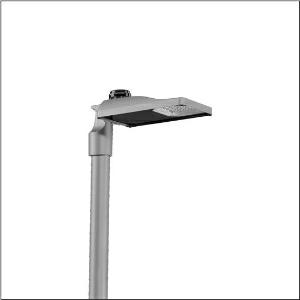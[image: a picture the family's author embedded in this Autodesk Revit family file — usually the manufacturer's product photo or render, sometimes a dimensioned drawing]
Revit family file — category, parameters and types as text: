
# Revit family: streetlight_sl_31_micro___st1_5a_5xh1p7bn08ca_d18d
name_source: partatom
category: Lighting Fixtures
units: mm (PartAtom-declared; Revit-internal decimal feet)

## family parameters
Cut with Voids When Loaded = No
Host = Face
Light Source = No
Part Type = Normal
Room Calculation Point = No
Round Connector Dimension = Use Diameter
Shared = No

## types (1)
- --- (1 x LED, 1150 lm, 10.3 W, 2200K)
    Apparent Load = 10 VA
    CIE Flux Codes = 22 53 95 100 100
    Color Rendering = 70
    Color Temperature = 2200K
    Default Elevation = 1800 mm
    Description = Streetlight SL 31 micro NEMA (7pin) mast luminaire for post-top, side-entry; light control with lens of PMMA; light distribution: ST1.5a, direct asymmetric distribution, for standard-compliant lighting for roads and squares; LED: luminous flux: 1.150lm, light colour: 722, colour temperature: 2200K; luminous efficacy: 111,7lm/W; control: overheat protection, intelligent temperature release in ECG and LED module, constant luminous flux control, time-dependent luminous flux control, flexible luminous flux parameterisation, pre-setting: linear dimming characteristic; luminaire housing, of diecast aluminium, SITECO metallic grey (DB 702S), corrosivity category C5 high according to DIN EN ISO 12944; cover of toughened safety glass, transparent, mast flange of diecast aluminium, SITECO metallic grey (DB 702S), spigot size: 76/60mm, mast flange included unmounted; cable length: 5,5m, connection cable pre-assembled; mains connection: 220..240V, AC, 50/60Hz; power consumption (at start of service life): 10,3W / (at end of service life): 10,6W / (with reduced operation 50%): 5,3W; protection rating (complete): IP66; insulation class (complete): insulation class I (protective earthing); impact resistance: IK10; certification: CE, ENEC, ENEC+, VDE, UKCA; permissible operating ambient temperature for outdoor applications: -40..+50°C; packaging unit: 1 piece

Light Distribution: ST1.5a
    Height = 76 mm
    Lamp = 1 x LED
    Lamp Light Flux = 1150 lm
    Lamp Power = 10.3 W
    Lamp count = 1
    Length = 467 mm
    Luminous efficacy = 112 lm/W
    Manufacturer = Siteco
    ModVariant = No
    Model = 5XH1P7BN08CA
    Mounting Place = Pole
    Mounting Type = Pole top
    Number of Poles = 1
    OnlyDefault = Yes
    Power Factor = 1
    Product Name = Streetlight SL 31 micro | ST1.5a
    Product group = mast luminaire | pylon top
    ProductGroupID = 6100
    Protection Class = Protection class I
    Protection Degree = IP 66
    RLX_Detail_Level = 1
    RLX_Emergency_Light_Flux = 0 lm
    RLX_Emergency_Type = 0
    RLX_Emergency_Type_DB = No
    RlxData = <blob elided: 26357 chars, md5=f9b57942>
    Socket = socket
    Standby Power = 0 W
    System Light Flux = 1150 lm
    System Power = 10 W
    Type Comments = factory setting: luminous flux: 100 % | dim-lin: 254 | 386 mA
    Type Image = l_1300305.jpg
    URL = http://relux.com
    VarID = @adj_011411
    Voltage = 0 V
    Weight = 0.00 kg
    Width = 265 mm

## geometry (parser evidence)
native form markers: Blend x4, Sweep x12
no freeform markers — native parametric forms only
